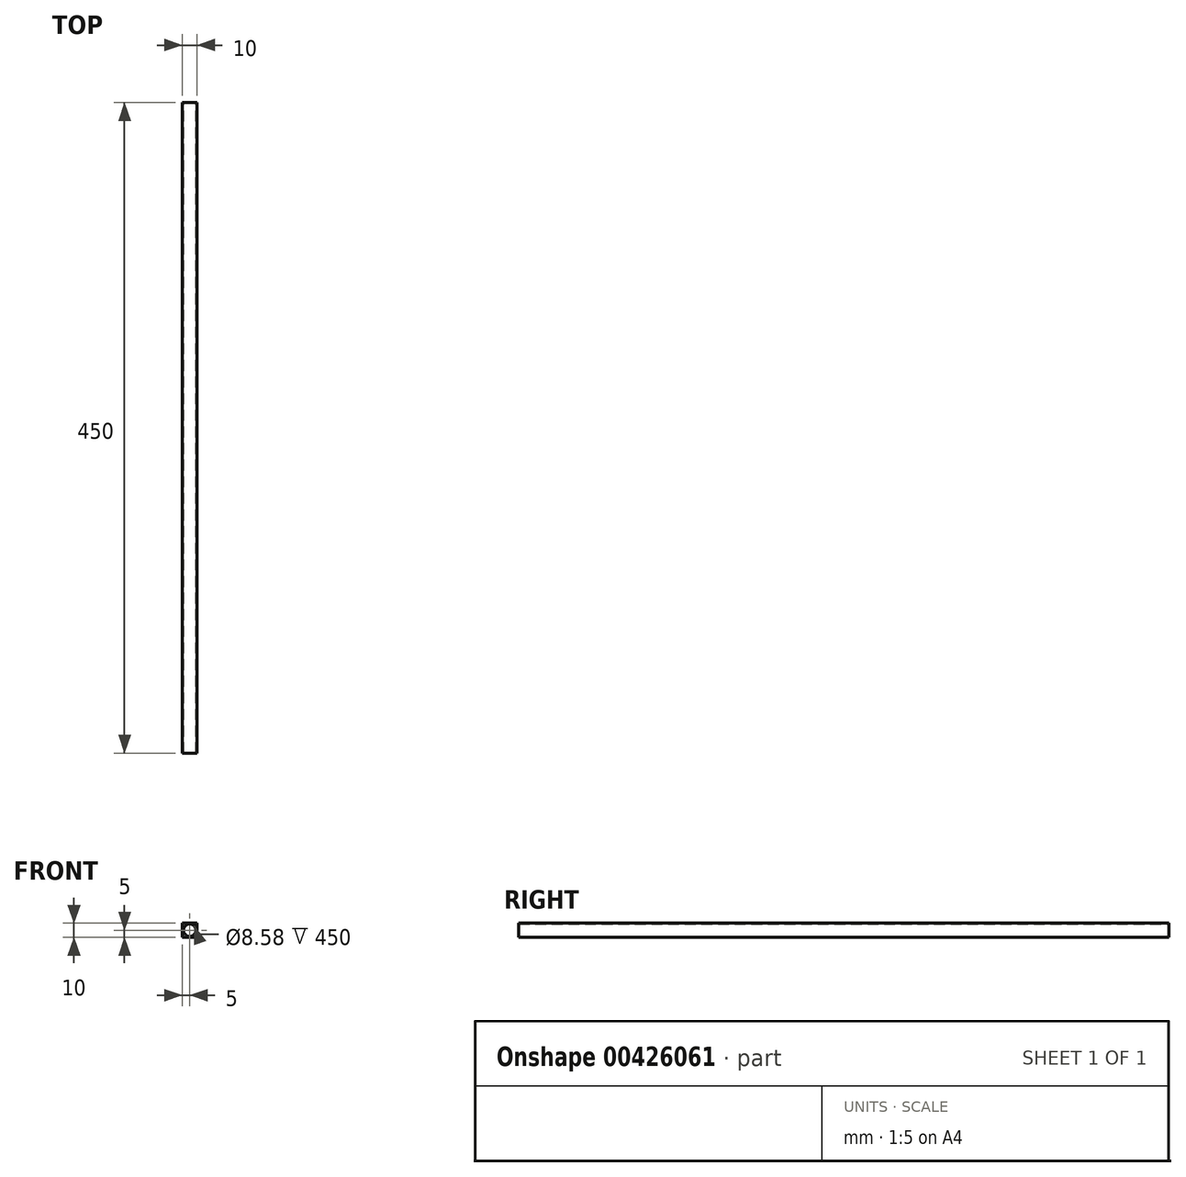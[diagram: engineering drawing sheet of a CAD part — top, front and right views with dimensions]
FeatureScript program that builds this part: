
annotation { "Feature Type Name" : "Feature", "Feature Type Description" : "" }
export const myFeature = defineFeature(function(context is Context, id is Id, definition is map)
    precondition{}
    {
        {
            var Q0;
            Q0=qCreatedBy(makeId("Front.planeOp"),FACE);
            var sketch = newSketch(context, id + "F0", { "sketchPlane" : qUnion([Q0])});
            skLineSegment(sketch, "E0.bottom", {"start": v(5, -5) * mm, "end": v(-5, -5) * mm});
            skLineSegment(sketch, "E0.top", {"start": v(5, 5) * mm, "end": v(-5, 5) * mm});
            skLineSegment(sketch, "E0.left", {"start": v(5, -5) * mm, "end": v(5, 5) * mm});
            skLineSegment(sketch, "E0.right", {"start": v(-5, -5) * mm, "end": v(-5, 5) * mm});
            skPoint(sketch, "E0.middle", {"position": v(0, 0) * mm});
            skCircle(sketch, "E1", {"center": v(0, 0) * mm, "radius": 4.29 * mm});
            skSolve(sketch);
        }
        {
            var Q0;
            Q0=qSketchRegion(id+"F0",true);
            extrude(context, id + "F1", {"entities" : qUnion([Q0]), "depth" : 450 * mm});
        }
    });
